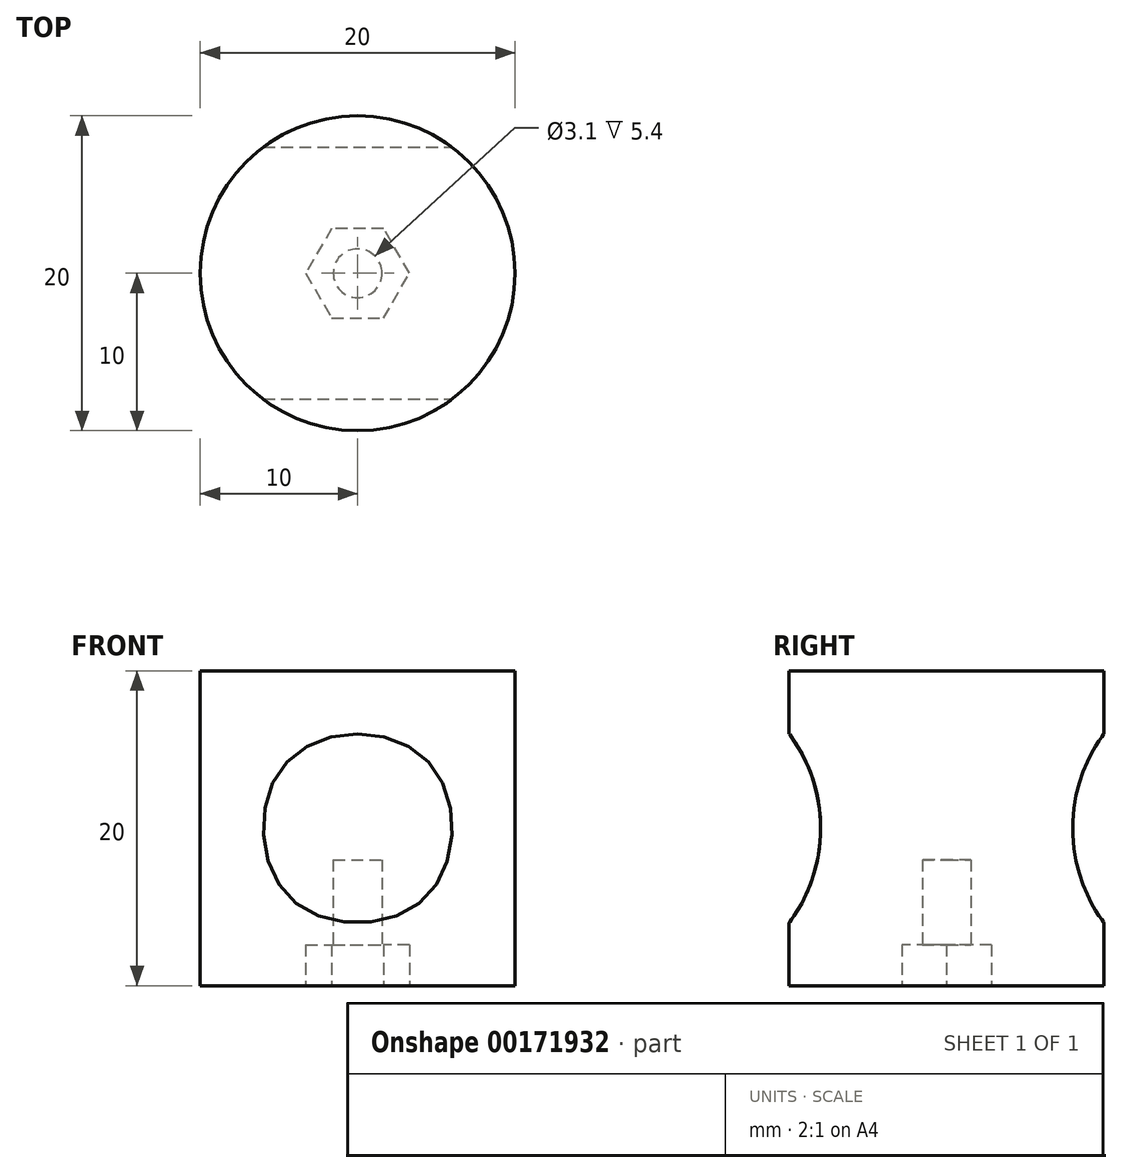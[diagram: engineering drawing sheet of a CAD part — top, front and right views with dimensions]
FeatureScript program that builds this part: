
annotation { "Feature Type Name" : "Feature", "Feature Type Description" : "" }
export const myFeature = defineFeature(function(context is Context, id is Id, definition is map)
    precondition{}
    {
        {
            var Q0;
            Q0=qCreatedBy(makeId("Top.planeOp"),FACE);
            var sketch = newSketch(context, id + "F0", { "sketchPlane" : qUnion([Q0])});
            skCircle(sketch, "E0", {"center": v(0, 0) * mm, "radius": 10 * mm});
            skSolve(sketch);
        }
        {
            var Q0;
            Q0 = qSketchRegion(id + "F0", true);
            extrude(context, id + "F1", {"entities" : qUnion([Q0]), "depth" : 20 * mm});
        }
        {
            var Q0;
            Q0=qCreatedBy(makeId("Right.planeOp"),FACE);
            var sketch = newSketch(context, id + "F2", { "sketchPlane" : qUnion([Q0])});
            skCircle(sketch, "E1", {"center": v(18, 10) * mm, "radius": 10 * mm});
            skCircle(sketch, "E2.MirrorC", {"center": v(-18, 10) * mm, "radius": 10 * mm});
            skSolve(sketch);
        }
        {
            var Q0;
            Q0 = qSketchRegion(id + "F2", true);
            extrude(context, id + "F3", {"entities" : qUnion([Q0]), "operationType" : NewBodyOperationType.REMOVE, "endBound" : BoundingType.SYMMETRIC, "oppositeDirection" : true, "depth" : 100 * mm});
        }
        {
            var Q0;
            Q0=makeQuery(id+"F1.opExtrude","CAP_FACE",FACE,{"disambiguationData":[OSD([sQuery(id+"F0.wireOp",EDGE,"E0")])],"isStart":true});
            var sketch = newSketch(context, id + "F4", { "sketchPlane" : qUnion([Q0])});
            skCircle(sketch, "E3.cCircle", {"center": v(0, 0) * mm, "radius": 2.85 * mm, "construction": true});
            skLineSegment(sketch, "E3.0", {"start": v(-1.65, 2.85) * mm, "end": v(1.65, 2.85) * mm});
            skLineSegment(sketch, "E3.1", {"start": v(1.65, 2.85) * mm, "end": v(3.3, 0) * mm});
            skLineSegment(sketch, "E3.2", {"start": v(3.3, 0) * mm, "end": v(1.65, -2.85) * mm});
            skLineSegment(sketch, "E3.3", {"start": v(1.65, -2.85) * mm, "end": v(-1.65, -2.85) * mm});
            skLineSegment(sketch, "E3.4", {"start": v(-1.65, -2.85) * mm, "end": v(-3.3, 0) * mm});
            skLineSegment(sketch, "E3.5", {"start": v(-3.3, 0) * mm, "end": v(-1.65, 2.85) * mm});
            skPoint(sketch, "E3.0.midPoint", {"position": v(0, 2.85) * mm});
            skCircle(sketch, "E4", {"center": v(0, 0) * mm, "radius": 1.55 * mm});
            skSolve(sketch);
        }
        {
            var Q0;
            Q0 = qSketchRegion(id + "F4", true);
            extrude(context, id + "F5", {"entities" : qUnion([Q0]), "operationType" : NewBodyOperationType.REMOVE, "oppositeDirection" : true, "depth" : 2.6 * mm});
        }
        {
            var Q0;
            Q0=makeQuery(id+"F5.boolean.opBoolean","SPLIT",FACE,{"disambiguationData":[TD([makeQuery(id+"F5.opExtrude","SWEPT_FACE",FACE,{"disambiguationData":[OSD([sQuery(id+"F4.wireOp",EDGE,"E4")])]})])],"derivedFrom":makeQuery(id+"F1.opExtrude","CAP_FACE",FACE,{"disambiguationData":[OSD([sQuery(id+"F0.wireOp",EDGE,"E0")])],"isStart":true})});
            extrude(context, id + "F6", {"entities" : qUnion([Q0]), "operationType" : NewBodyOperationType.REMOVE, "oppositeDirection" : true, "depth" : 8 * mm});
        }
    });
